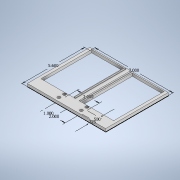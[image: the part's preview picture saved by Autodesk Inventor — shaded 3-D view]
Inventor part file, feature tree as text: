
AUTODESK INVENTOR PART (.ipt)
format: ipt  version: 2020 (Build 240168000, 168)  size: 153,600 bytes
history: native  units: in
note: dims shown in document units (in); Inventor stores cm internally (conversion verified against a paired STEP export)
features: sketch x3, extrude x3, hole x1
ambient origin geometry x8: Origin, YZ Plane, XZ Plane, XY Plane, X Axis, Y Axis, Z Axis, Center Point
bodies: Solid1 (feature_tree)
feature tree (7):
  sketch  "Sketch1"  dims[d0=7.0in d1=5.6in]
  extrude  "Extrusion1"  Depth=5.6in
  hole  "Hole1"  [1 undecoded]
  extrude  "Extrusion2"  Depth=0.05in
  extrude  "Extrusion4"  Depth=0.05in
  sketch  "Sketch2"  dims[d2=1.0in d3=2.0in]
  sketch  "Sketch3"  dims[d4=0.325in d5=0.5in d6=2.0in d7=0.25in d8=0.0in d9=0.266in d10=0.75in d11=0.438in d12=0.25in d13=0.5635in d14=1.0in d15=0.8108in d16=0.25in d17=0.1in d18=2.8654in d19=4.5299in d20=0.25in d21=2.865in d22=4.5299in d23=0.25in d24=0.0in d26=0.1in d27=0.1in d30=0.1in d31=0.1in d32=0.05in d33=0.0in]
note: 1 required parameter value undecoded (feature->parameter linkage not recoverable at this tier; creation-order binding heuristic only, values carry confidence <= 0.55)
